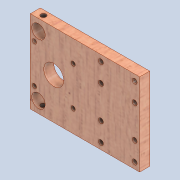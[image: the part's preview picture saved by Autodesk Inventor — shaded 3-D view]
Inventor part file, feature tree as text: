
AUTODESK INVENTOR PART (.ipt)
format: ipt  version: 2020 (Build 240168000, 168)  size: 353,280 bytes
history: native  units: mm
features: sketch x6, other x6, extrude x4, reference x4, hole x3, pattern_linear x2
ambient origin geometry x8: Origin, YZ Plane, XZ Plane, XY Plane, X Axis, Y Axis, Z Axis, Center Point
bodies: Solid1 (feature_tree)
feature tree (25):
  extrude  "Extrusion1"  Depth=66.0mm
  extrude  "Extrusion4"  TaperAngle=0.0deg  [1 undecoded]
  extrude  "Extrusion5"  TaperAngle=0.0deg  [1 undecoded]
  extrude  "Extrusion6"  Depth=9.0mm
  hole  "Hole1"  [1 undecoded]
  pattern_linear  "Rectangular Pattern1"  Spacing1=18.748842mm  [1 undecoded]
  pattern_linear  "Rectangular Pattern2"  Spacing1=3.5mm  [1 undecoded]
  hole  "Hole2"  [1 undecoded]
  hole  "Hole3"  [1 undecoded]
  sketch  "Sketch1"  dims[d0=87.5mm d1=66.0mm]
  sketch  "Sketch4"  dims[d2=8.0mm d3=0.0mm d19=0.0mm d20=0.0mm]
  sketch  "Sketch6"  dims[d24=16.0mm d25=0.0mm d26=0.0mm]
  reference  "Reference7"
  reference  "Reference8"
  sketch  "Sketch8"  dims[d27=6.5mm d28=9.0mm]
  reference  "Reference9"
  reference  "Reference10"
  sketch  "Sketch9"  dims[d29=10.8mm d30=9.0mm]
  sketch  "Sketch10"  dims[d31=0.0mm d32=0.0mm d33=18.748842mm d35=3.5mm d36=31.0mm d38=5.0mm d39=15.0mm d40=26.0mm d41=15.0mm d42=4.0mm d43=4.0mm d44=6.0mm d45=4.0mm d46=2.0mm d47=90.0deg d48=8.0mm d49=20.594885mm d50=20.0mm d52=15.0mm d53=20.0mm d55=41.0mm d56=20.0mm d58=27.0mm d59=6.5mm d60=4.134mm d61=5.0mm d62=4.0mm d63=2.0mm d64=90.0deg d65=7.45mm d66=20.594885mm d67=4.134mm d68=5.0mm d69=4.0mm d70=2.0mm d71=90.0deg d72=7.45mm d73=20.594885mm]
  parser-record x1  (decoder bookkeeping rows leaked as tree rows — omitted from the tree; the rows remain in map.json)
  other  "0005-00-00 Ansamblu_General.iam"
  other  "0005-10-1001 NEMA17 - Motor de passo.ipt:23"
  other  "0005-10-04 Z axis and extruder.iam"
  other  "0005-10-10-1003 LeadScrew 8mm x 2mmPitch.ipt:21"
  other  "0005-10-1002  Hub.ipt:22"
note: 7 required parameter values undecoded (feature->parameter linkage not recoverable at this tier; creation-order binding heuristic only, values carry confidence <= 0.55)
note: 1 file-system path scrubbed to <path> (originals preserved in map.json)
